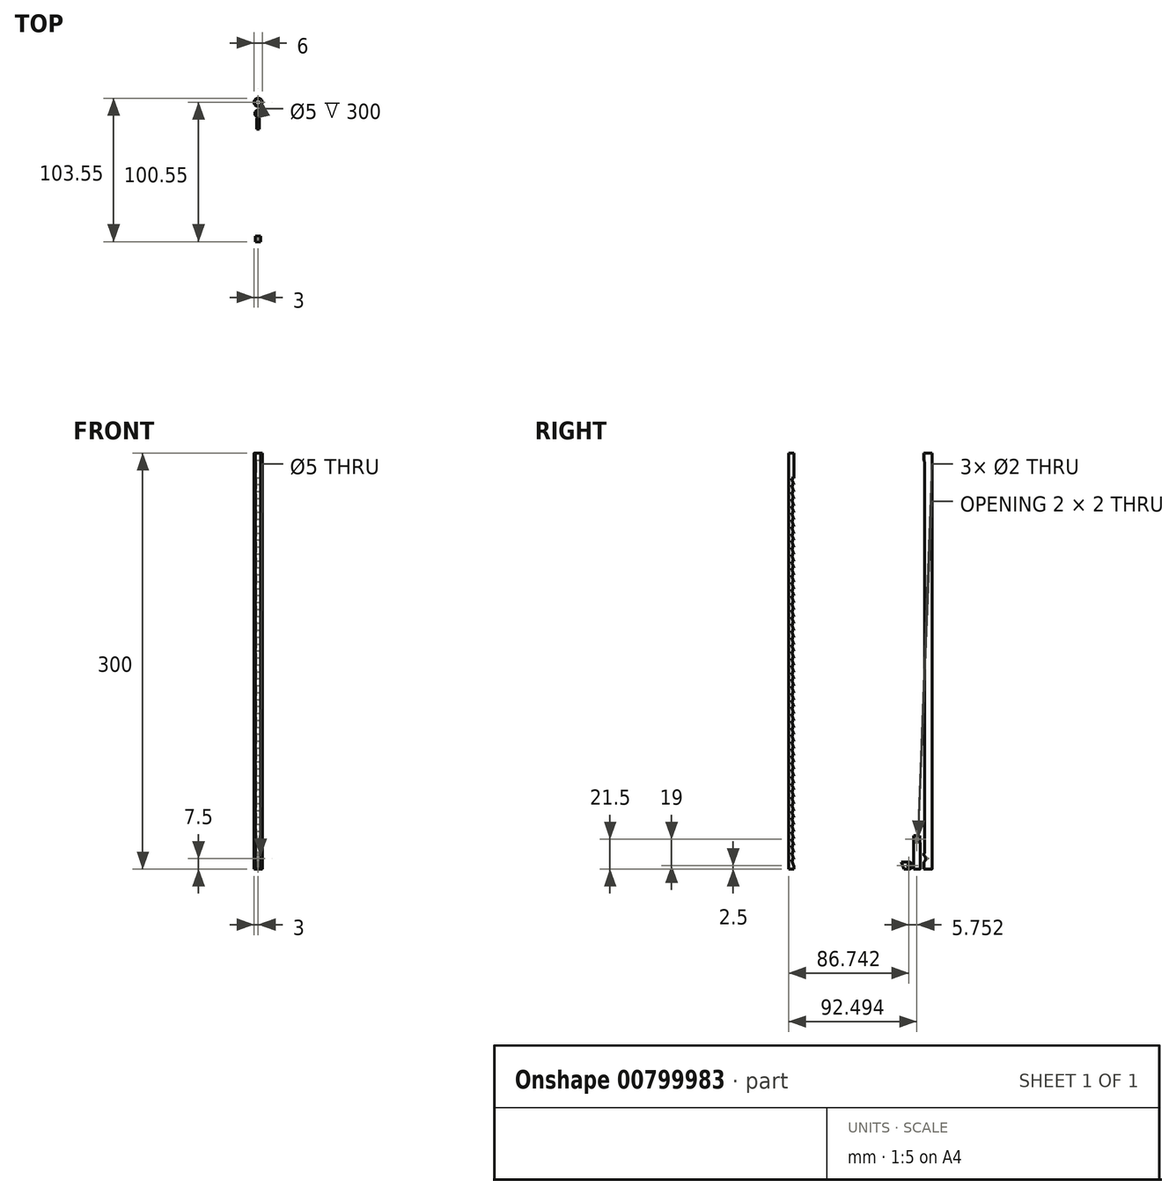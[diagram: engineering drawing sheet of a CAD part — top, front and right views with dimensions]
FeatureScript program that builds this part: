
annotation { "Feature Type Name" : "Feature", "Feature Type Description" : "" }
export const myFeature = defineFeature(function(context is Context, id is Id, definition is map)
    precondition{}
    {
        {
            var Q0;
            Q0=qCreatedBy(makeId("Top.planeOp"),FACE);
            var sketch = newSketch(context, id + "F0", { "sketchPlane" : qUnion([Q0])});
            skCircle(sketch, "E0", {"center": v(0, 3) * mm, "radius": 3 * mm});
            skCircle(sketch, "E1", {"center": v(0, 3) * mm, "radius": 2.5 * mm});
            skSolve(sketch);
        }
        {
            var Q0;
            Q0 = qSketchRegion(id + "F0", true);
            extrude(context, id + "F1", {"entities" : qUnion([Q0]), "depth" : 300 * mm, "offsetDistance" : 25 * mm});
        }
        {
            var Q0;
            Q0=qCreatedBy(makeId("Front.planeOp"),FACE);
            var sketch = newSketch(context, id + "F2", { "sketchPlane" : qUnion([Q0])});
            skCircle(sketch, "E2", {"center": v(0, 7.5) * mm, "radius": 2.5 * mm});
            skCircle(sketch, "E3", {"center": v(0, 17.5) * mm, "radius": 1.5 * mm});
            skCircle(sketch, "E4", {"center": v(0, 293.5) * mm, "radius": 1.5 * mm});
            skLineSegment(sketch, "E5", {"start": v(0, 0) * mm, "end": v(0, 300) * mm});
            skSolve(sketch);
        }
        {
            var Q0;
            Q0 = qSketchRegion(id + "F0", true);
            var Q1;
            Q1=sQuery(id+"F2.wireOp",EDGE,"E2");
            extrude(context, id + "F3", {"entities" : qUnion([Q0]), "operationType" : NewBodyOperationType.REMOVE, "surfaceEntities" : qUnion([Q1]), "oppositeDirection" : true, "depth" : 25 * mm, "offsetDistance" : 25 * mm});
        }
        {
            var Q0;
            Q0=sQuery(id+"F2.wireOp",VERTEX,"E2.center");
            var Q1;
            Q1=makeQuery(id+"F1.opExtrude","SWEPT_BODY",BODY,{"disambiguationData":[OSD([sQuery(id+"F0.wireOp",EDGE,"E0"),sQuery(id+"F0.wireOp",EDGE,"E1")])]});
            hole(context, id + "F4", {"style" : HoleStyle.SIMPLE, "endStyle" : HoleEndStyle.BLIND, "holeDiameter" : 5 * mm, "majorDiameter" : 5 * mm, "holeDepth" : 2 * mm, "isTappedThrough" : true, "tappedDepth" : 12 * mm, "tapClearance" : 3, "locations" : qUnion([Q0]), "scope" : qUnion([Q1])});
        }
        {
            var Q0;
            Q0 = qSketchRegion(id + "F2", true);
            var sketch = newSketch(context, id + "F5", { "sketchPlane" : qUnion([Q0])});
            skLineSegment(sketch, "E6.bottom", {"start": v(-1.5, 11.4) * mm, "end": v(1.5, 11.4) * mm});
            skLineSegment(sketch, "E6.top", {"start": v(-1.5, 293.43) * mm, "end": v(1.5, 293.43) * mm});
            skLineSegment(sketch, "E6.left", {"start": v(-1.5, 11.4) * mm, "end": v(-1.5, 293.43) * mm});
            skLineSegment(sketch, "E6.right", {"start": v(1.5, 11.4) * mm, "end": v(1.5, 293.43) * mm});
            skLineSegment(sketch, "E7", {"start": v(0, 10) * mm, "end": v(0, 300) * mm});
            skLineSegment(sketch, "E8", {"start": v(0, 0) * mm, "end": v(0, 5) * mm});
            skSolve(sketch);
        }
        {
            var Q0;
            {var subQ0=sQuery(id+"F2.wireOp",EDGE,"E5");var subQ1=sQuery(id+"F2.wireOp",EDGE,"E3");var subQ2=makeQuery(id+"F2.imprint","INTERSECT",VERTEX,{"disambiguationData":[OD(0.0)],"derivedFrom":[subQ1,subQ0]});Q0=makeQuery(id+"F2.imprint","IMPRINT",FACE,{"disambiguationData":[TD([[makeQuery(id+"F2.imprint","IMPRINT",EDGE,{"disambiguationData":[TD([[subQ2,1.0]])],"derivedFrom":subQ1}),1.0]])]});}
            var Q1;
            {var subQ0=sQuery(id+"F2.wireOp",EDGE,"E5");var subQ1=sQuery(id+"F2.wireOp",EDGE,"E3");var subQ2=makeQuery(id+"F2.imprint","INTERSECT",VERTEX,{"disambiguationData":[OD(0.0)],"derivedFrom":[subQ1,subQ0]});var subQ5=makeQuery(id+"F2.imprint","IMPRINT",EDGE,{"disambiguationData":[TD([[subQ2,1.0]])],"derivedFrom":subQ1});var subQ9=sQuery(id+"F5.wireOp",EDGE,"E6.left");var subQ10=makeQuery(id+"F5.imprint","INTERSECT",VERTEX,{"disambiguationData":[OD(1.0)],"derivedFrom":[subQ5,subQ9]});Q1=makeQuery(id+"F5.imprint","IMPRINT",FACE,{"disambiguationData":[TD([[makeQuery(id+"F5.imprint","IMPRINT",EDGE,{"disambiguationData":[TD([[subQ10,-1.0]])],"derivedFrom":subQ9}),-1.0]])]});}
            var Q2;
            {var subQ0=sQuery(id+"F2.wireOp",EDGE,"E5");var subQ1=sQuery(id+"F2.wireOp",EDGE,"E3");var subQ2=makeQuery(id+"F2.imprint","INTERSECT",VERTEX,{"disambiguationData":[OD(0.0)],"derivedFrom":[subQ1,subQ0]});Q2=makeQuery(id+"F2.imprint","IMPRINT",FACE,{"disambiguationData":[TD([[makeQuery(id+"F2.imprint","IMPRINT",EDGE,{"disambiguationData":[TD([[subQ2,-1.0]])],"derivedFrom":subQ1}),1.0]])]});}
            extrude(context, id + "F6", {"entities" : qUnion([Q0, Q1, Q2]), "operationType" : NewBodyOperationType.REMOVE, "depth" : 2 * mm, "offsetDistance" : 25 * mm});
        }
        {
            var Q0;
            {var subQ0=sQuery(id+"F2.wireOp",EDGE,"E5");var subQ1=sQuery(id+"F2.wireOp",EDGE,"E3");var subQ2=makeQuery(id+"F2.imprint","INTERSECT",VERTEX,{"disambiguationData":[OD(0.0)],"derivedFrom":[subQ1,subQ0]});Q0=makeQuery(id+"F2.imprint","IMPRINT",FACE,{"disambiguationData":[TD([[makeQuery(id+"F2.imprint","IMPRINT",EDGE,{"disambiguationData":[TD([[subQ2,-1.0]])],"derivedFrom":subQ1}),1.0]])]});}
            var Q1;
            {var subQ0=sQuery(id+"F2.wireOp",EDGE,"E5");var subQ1=sQuery(id+"F2.wireOp",EDGE,"E3");var subQ2=makeQuery(id+"F2.imprint","INTERSECT",VERTEX,{"disambiguationData":[OD(0.0)],"derivedFrom":[subQ1,subQ0]});Q1=makeQuery(id+"F2.imprint","IMPRINT",FACE,{"disambiguationData":[TD([[makeQuery(id+"F2.imprint","IMPRINT",EDGE,{"disambiguationData":[TD([[subQ2,1.0]])],"derivedFrom":subQ1}),1.0]])]});}
            var Q2;
            {var subQ0=sQuery(id+"F5.wireOp",EDGE,"E6.right");var subQ1=sQuery(id+"F2.wireOp",EDGE,"E5");var subQ7=sQuery(id+"F2.wireOp",EDGE,"E3");var subQ8=makeQuery(id+"F2.imprint","INTERSECT",VERTEX,{"disambiguationData":[OD(0.0)],"derivedFrom":[subQ7,subQ1]});var subQ10=makeQuery(id+"F2.imprint","IMPRINT",EDGE,{"disambiguationData":[TD([[subQ8,-1.0]])],"derivedFrom":subQ7});var subQ11=makeQuery(id+"F5.imprint","INTERSECT",VERTEX,{"disambiguationData":[OD(1.0)],"derivedFrom":[subQ10,subQ0]});Q2=makeQuery(id+"F5.imprint","IMPRINT",FACE,{"disambiguationData":[TD([[makeQuery(id+"F5.imprint","IMPRINT",EDGE,{"disambiguationData":[TD([[subQ11,-1.0]])],"derivedFrom":subQ0}),1.0]])]});}
            var Q3;
            {var subQ0=sQuery(id+"F5.wireOp",EDGE,"E6.left");var subQ1=sQuery(id+"F2.wireOp",EDGE,"E5");var subQ7=sQuery(id+"F2.wireOp",EDGE,"E3");var subQ8=makeQuery(id+"F2.imprint","INTERSECT",VERTEX,{"disambiguationData":[OD(0.0)],"derivedFrom":[subQ7,subQ1]});var subQ10=makeQuery(id+"F2.imprint","IMPRINT",EDGE,{"disambiguationData":[TD([[subQ8,1.0]])],"derivedFrom":subQ7});var subQ11=makeQuery(id+"F5.imprint","INTERSECT",VERTEX,{"disambiguationData":[OD(1.0)],"derivedFrom":[subQ10,subQ0]});Q3=makeQuery(id+"F5.imprint","IMPRINT",FACE,{"disambiguationData":[TD([[makeQuery(id+"F5.imprint","IMPRINT",EDGE,{"disambiguationData":[TD([[subQ11,-1.0]])],"derivedFrom":subQ0}),-1.0]])]});}
            var Q4;
            {var subQ0=sQuery(id+"F2.wireOp",EDGE,"E5");var subQ1=sQuery(id+"F2.wireOp",EDGE,"E4");var subQ2=makeQuery(id+"F2.imprint","INTERSECT",VERTEX,{"disambiguationData":[OD(0.0)],"derivedFrom":[subQ1,subQ0]});Q4=makeQuery(id+"F2.imprint","IMPRINT",FACE,{"disambiguationData":[TD([[makeQuery(id+"F2.imprint","IMPRINT",EDGE,{"disambiguationData":[TD([[subQ2,-1.0]])],"derivedFrom":subQ1}),1.0]])]});}
            var Q5;
            {var subQ0=sQuery(id+"F2.wireOp",EDGE,"E5");var subQ1=sQuery(id+"F2.wireOp",EDGE,"E4");var subQ2=makeQuery(id+"F2.imprint","INTERSECT",VERTEX,{"disambiguationData":[OD(0.0)],"derivedFrom":[subQ1,subQ0]});Q5=makeQuery(id+"F2.imprint","IMPRINT",FACE,{"disambiguationData":[TD([[makeQuery(id+"F2.imprint","IMPRINT",EDGE,{"disambiguationData":[TD([[subQ2,1.0]])],"derivedFrom":subQ1}),1.0]])]});}
            extrude(context, id + "F7", {"entities" : qUnion([Q0, Q1, Q2, Q3, Q4, Q5]), "operationType" : NewBodyOperationType.REMOVE, "oppositeDirection" : true, "depth" : 2 * mm, "offsetDistance" : 25 * mm});
        }
        {
            var Q0;
            Q0=qCreatedBy(makeId("Top.planeOp"),FACE);
            var sketch = newSketch(context, id + "F8", { "sketchPlane" : qUnion([Q0])});
            skCircle(sketch, "E9", {"center": v(0, -5.06) * mm, "radius": 2.45 * mm});
            skSolve(sketch);
        }
        {
            var Q0;
            Q0 = qSketchRegion(id + "F8", true);
            extrude(context, id + "F9", {"entities" : qUnion([Q0]), "depth" : 24 * mm, "offsetDistance" : 25 * mm});
        }
        {
            var Q0;
            Q0=makeQuery(id+"F9.opExtrude","CAP_FACE",FACE,{"disambiguationData":[OSD([sQuery(id+"F8.wireOp",EDGE,"E9")])],"isStart":false});
            var sketch = newSketch(context, id + "F10", { "sketchPlane" : qUnion([Q0])});
            skLineSegment(sketch, "E10.bottom", {"start": v(1, -8.94) * mm, "end": v(-1, -8.94) * mm});
            skLineSegment(sketch, "E10.top", {"start": v(1, -1.17) * mm, "end": v(-1, -1.17) * mm});
            skLineSegment(sketch, "E10.left", {"start": v(1, -8.94) * mm, "end": v(1, -1.17) * mm});
            skLineSegment(sketch, "E10.right", {"start": v(-1, -8.94) * mm, "end": v(-1, -1.17) * mm});
            skPoint(sketch, "E10.middle", {"position": v(0, -5.06) * mm});
            skSolve(sketch);
        }
        {
            var Q0;
            Q0 = qSketchRegion(id + "F10", true);
            extrude(context, id + "F11", {"entities" : qUnion([Q0]), "operationType" : NewBodyOperationType.REMOVE, "oppositeDirection" : true, "depth" : 5 * mm, "offsetDistance" : 25 * mm});
        }
        {
            var Q0;
            Q0=qCreatedBy(makeId("Right.planeOp"),FACE);
            var sketch = newSketch(context, id + "F12", { "sketchPlane" : qUnion([Q0])});
            skCircle(sketch, "E11", {"center": v(-5.06, 21.5) * mm, "radius": 1 * mm});
            skLineSegment(sketch, "E12", {"start": v(-2.6, 19) * mm, "end": v(-2.6, 0) * mm});
            skLineSegment(sketch, "E13", {"start": v(-7.5, 0) * mm, "end": v(-7.5, 19) * mm});
            skSolve(sketch);
        }
        {
            var Q0;
            Q0 = qSketchRegion(id + "F12", true);
            extrude(context, id + "F13", {"entities" : qUnion([Q0]), "operationType" : NewBodyOperationType.REMOVE, "depth" : 25 * mm, "offsetDistance" : 25 * mm, "hasSecondDirection" : true, "secondDirectionOppositeDirection" : true, "secondDirectionDepth" : 25 * mm});
        }
        {
            var Q0;
            Q0=qCreatedBy(makeId("Top.planeOp"),FACE);
            var sketch = newSketch(context, id + "F14", { "sketchPlane" : qUnion([Q0])});
            skLineSegment(sketch, "E14.bottom", {"start": v(1, -16.3) * mm, "end": v(-1, -16.3) * mm});
            skLineSegment(sketch, "E14.top", {"start": v(1, -8.3) * mm, "end": v(-1, -8.3) * mm});
            skLineSegment(sketch, "E14.left", {"start": v(1, -16.3) * mm, "end": v(1, -8.3) * mm});
            skLineSegment(sketch, "E14.right", {"start": v(-1, -16.3) * mm, "end": v(-1, -8.3) * mm});
            skPoint(sketch, "E14.middle", {"position": v(0, -12.3) * mm});
            skSolve(sketch);
        }
        {
            var Q0;
            Q0 = qSketchRegion(id + "F14", true);
            extrude(context, id + "F15", {"entities" : qUnion([Q0]), "depth" : 5 * mm, "offsetDistance" : 25 * mm});
        }
        {
            var Q0;
            Q0=makeQuery(id+"F15.opExtrude","SWEPT_FACE",FACE,{"disambiguationData":[OSD([sQuery(id+"F14.wireOp",EDGE,"E14.left")])]});
            cPlane(context, id + "F16", {"entities" : qUnion([Q0]), "cplaneType" : CPlaneType.OFFSET, "offset" : 0 * mm, "width" : 150 * mm, "height" : 150 * mm});
        }
        {
            var Q0;
            Q0=qCreatedBy(id+"F16.planeOp",FACE);
            var sketch = newSketch(context, id + "F17", { "sketchPlane" : qUnion([Q0])});
            skCircle(sketch, "E15", {"center": v(-10.8, 2.5) * mm, "radius": 2.5 * mm});
            skSolve(sketch);
        }
        {
            var Q0;
            Q0=makeQuery(id+"F15.opExtrude","CAP_EDGE",EDGE,{"disambiguationData":[OSD([sQuery(id+"F14.wireOp",EDGE,"E14.top")])],"isStart":true});
            var Q1;
            Q1=makeQuery(id+"F15.opExtrude","CAP_EDGE",EDGE,{"disambiguationData":[OSD([sQuery(id+"F14.wireOp",EDGE,"E14.top")])],"isStart":false});
            fillet(context, id + "F18", {"entities" : qUnion([Q0, Q1]), "radius" : 2.5 * mm, "tangentPropagation" : true, "allowEdgeOverflow" : false});
        }
        {
            var Q0;
            Q0=sQuery(id+"F17.wireOp",VERTEX,"E15.center");
            var Q1;
            Q1=makeQuery(id+"F15.opExtrude","SWEPT_BODY",BODY,{"disambiguationData":[OSD([sQuery(id+"F14.wireOp",EDGE,"E14.bottom"),sQuery(id+"F14.wireOp",EDGE,"E14.top"),sQuery(id+"F14.wireOp",EDGE,"E14.left"),sQuery(id+"F14.wireOp",EDGE,"E14.right")])]});
            hole(context, id + "F19", {"style" : HoleStyle.SIMPLE, "endStyle" : HoleEndStyle.THROUGH, "holeDiameter" : 2 * mm, "majorDiameter" : 5 * mm, "isTappedThrough" : true, "tappedDepth" : 12 * mm, "tapClearance" : 3, "locations" : qUnion([Q0]), "scope" : qUnion([Q1])});
        }
        {
            var Q0;
            Q0=makeQuery(id+"F15.opExtrude","CAP_EDGE",EDGE,{"disambiguationData":[OSD([sQuery(id+"F14.wireOp",EDGE,"E14.bottom")])],"isStart":true});
            chamfer(context, id + "F20", {"entities" : qUnion([Q0]), "chamferType" : ChamferType.TWO_OFFSETS, "width1" : 2 * mm, "oppositeDirection" : false, "width2" : 5 * mm, "tangentPropagation" : true});
        }
        {
            var Q0;
            Q0=qCreatedBy(makeId("Right.planeOp"),FACE);
            var sketch = newSketch(context, id + "F21", { "sketchPlane" : qUnion([Q0])});
            skLineSegment(sketch, "E16.bottom", {"start": v(-97.55, 0) * mm, "end": v(-93.65, 0) * mm});
            skLineSegment(sketch, "E16.top", {"start": v(-97.55, 300) * mm, "end": v(-93.65, 300) * mm});
            skLineSegment(sketch, "E16.left", {"start": v(-97.55, 0) * mm, "end": v(-97.55, 300) * mm});
            skLineSegment(sketch, "E16.right", {"start": v(-93.65, 0) * mm, "end": v(-93.65, 300) * mm});
            skLineSegment(sketch, "E17", {"start": v(-93.65, 7) * mm, "end": v(-95.65, 7) * mm});
            skLineSegment(sketch, "E18", {"start": v(-95.65, 7) * mm, "end": v(-93.65, 2) * mm});
            skLineSegment(sketch, "E19.0.1.0", {"start": v(-93.65, 12) * mm, "end": v(-95.65, 12) * mm});
            skLineSegment(sketch, "E19.0.1.1", {"start": v(-95.65, 12) * mm, "end": v(-93.65, 7) * mm});
            skLineSegment(sketch, "E19.0.2.0", {"start": v(-93.65, 17) * mm, "end": v(-95.65, 17) * mm});
            skLineSegment(sketch, "E19.0.2.1", {"start": v(-95.65, 17) * mm, "end": v(-93.65, 12) * mm});
            skLineSegment(sketch, "E19.0.3.0", {"start": v(-93.65, 22) * mm, "end": v(-95.65, 22) * mm});
            skLineSegment(sketch, "E19.0.3.1", {"start": v(-95.65, 22) * mm, "end": v(-93.65, 17) * mm});
            skLineSegment(sketch, "E19.0.4.0", {"start": v(-93.65, 27) * mm, "end": v(-95.65, 27) * mm});
            skLineSegment(sketch, "E19.0.4.1", {"start": v(-95.65, 27) * mm, "end": v(-93.65, 22) * mm});
            skLineSegment(sketch, "E19.0.5.0", {"start": v(-93.65, 32) * mm, "end": v(-95.65, 32) * mm});
            skLineSegment(sketch, "E19.0.5.1", {"start": v(-95.65, 32) * mm, "end": v(-93.65, 27) * mm});
            skLineSegment(sketch, "E19.0.6.0", {"start": v(-93.65, 37) * mm, "end": v(-95.65, 37) * mm});
            skLineSegment(sketch, "E19.0.6.1", {"start": v(-95.65, 37) * mm, "end": v(-93.65, 32) * mm});
            skLineSegment(sketch, "E19.0.7.0", {"start": v(-93.65, 42) * mm, "end": v(-95.65, 42) * mm});
            skLineSegment(sketch, "E19.0.7.1", {"start": v(-95.65, 42) * mm, "end": v(-93.65, 37) * mm});
            skLineSegment(sketch, "E19.0.8.0", {"start": v(-93.65, 47) * mm, "end": v(-95.65, 47) * mm});
            skLineSegment(sketch, "E19.0.8.1", {"start": v(-95.65, 47) * mm, "end": v(-93.65, 42) * mm});
            skLineSegment(sketch, "E19.0.9.0", {"start": v(-93.65, 52) * mm, "end": v(-95.65, 52) * mm});
            skLineSegment(sketch, "E19.0.9.1", {"start": v(-95.65, 52) * mm, "end": v(-93.65, 47) * mm});
            skLineSegment(sketch, "E19.0.10.0", {"start": v(-93.65, 57) * mm, "end": v(-95.65, 57) * mm});
            skLineSegment(sketch, "E19.0.10.1", {"start": v(-95.65, 57) * mm, "end": v(-93.65, 52) * mm});
            skLineSegment(sketch, "E19.0.11.0", {"start": v(-93.65, 62) * mm, "end": v(-95.65, 62) * mm});
            skLineSegment(sketch, "E19.0.11.1", {"start": v(-95.65, 62) * mm, "end": v(-93.65, 57) * mm});
            skLineSegment(sketch, "E19.0.12.0", {"start": v(-93.65, 67) * mm, "end": v(-95.65, 67) * mm});
            skLineSegment(sketch, "E19.0.12.1", {"start": v(-95.65, 67) * mm, "end": v(-93.65, 62) * mm});
            skLineSegment(sketch, "E19.0.13.0", {"start": v(-93.65, 72) * mm, "end": v(-95.65, 72) * mm});
            skLineSegment(sketch, "E19.0.13.1", {"start": v(-95.65, 72) * mm, "end": v(-93.65, 67) * mm});
            skLineSegment(sketch, "E19.0.14.0", {"start": v(-93.65, 77) * mm, "end": v(-95.65, 77) * mm});
            skLineSegment(sketch, "E19.0.14.1", {"start": v(-95.65, 77) * mm, "end": v(-93.65, 72) * mm});
            skLineSegment(sketch, "E19.0.15.0", {"start": v(-93.65, 82) * mm, "end": v(-95.65, 82) * mm});
            skLineSegment(sketch, "E19.0.15.1", {"start": v(-95.65, 82) * mm, "end": v(-93.65, 77) * mm});
            skLineSegment(sketch, "E19.0.16.0", {"start": v(-93.65, 87) * mm, "end": v(-95.65, 87) * mm});
            skLineSegment(sketch, "E19.0.16.1", {"start": v(-95.65, 87) * mm, "end": v(-93.65, 82) * mm});
            skLineSegment(sketch, "E19.0.17.0", {"start": v(-93.65, 92) * mm, "end": v(-95.65, 92) * mm});
            skLineSegment(sketch, "E19.0.17.1", {"start": v(-95.65, 92) * mm, "end": v(-93.65, 87) * mm});
            skLineSegment(sketch, "E19.0.18.0", {"start": v(-93.65, 97) * mm, "end": v(-95.65, 97) * mm});
            skLineSegment(sketch, "E19.0.18.1", {"start": v(-95.65, 97) * mm, "end": v(-93.65, 92) * mm});
            skLineSegment(sketch, "E19.0.19.0", {"start": v(-93.65, 102) * mm, "end": v(-95.65, 102) * mm});
            skLineSegment(sketch, "E19.0.19.1", {"start": v(-95.65, 102) * mm, "end": v(-93.65, 97) * mm});
            skLineSegment(sketch, "E19.0.20.0", {"start": v(-93.65, 107) * mm, "end": v(-95.65, 107) * mm});
            skLineSegment(sketch, "E19.0.20.1", {"start": v(-95.65, 107) * mm, "end": v(-93.65, 102) * mm});
            skLineSegment(sketch, "E19.0.21.0", {"start": v(-93.65, 112) * mm, "end": v(-95.65, 112) * mm});
            skLineSegment(sketch, "E19.0.21.1", {"start": v(-95.65, 112) * mm, "end": v(-93.65, 107) * mm});
            skLineSegment(sketch, "E19.0.22.0", {"start": v(-93.65, 117) * mm, "end": v(-95.65, 117) * mm});
            skLineSegment(sketch, "E19.0.22.1", {"start": v(-95.65, 117) * mm, "end": v(-93.65, 112) * mm});
            skLineSegment(sketch, "E19.0.23.0", {"start": v(-93.65, 122) * mm, "end": v(-95.65, 122) * mm});
            skLineSegment(sketch, "E19.0.23.1", {"start": v(-95.65, 122) * mm, "end": v(-93.65, 117) * mm});
            skLineSegment(sketch, "E19.0.24.0", {"start": v(-93.65, 127) * mm, "end": v(-95.65, 127) * mm});
            skLineSegment(sketch, "E19.0.24.1", {"start": v(-95.65, 127) * mm, "end": v(-93.65, 122) * mm});
            skLineSegment(sketch, "E19.0.25.0", {"start": v(-93.65, 132) * mm, "end": v(-95.65, 132) * mm});
            skLineSegment(sketch, "E19.0.25.1", {"start": v(-95.65, 132) * mm, "end": v(-93.65, 127) * mm});
            skLineSegment(sketch, "E19.0.26.0", {"start": v(-93.65, 137) * mm, "end": v(-95.65, 137) * mm});
            skLineSegment(sketch, "E19.0.26.1", {"start": v(-95.65, 137) * mm, "end": v(-93.65, 132) * mm});
            skLineSegment(sketch, "E19.0.27.0", {"start": v(-93.65, 142) * mm, "end": v(-95.65, 142) * mm});
            skLineSegment(sketch, "E19.0.27.1", {"start": v(-95.65, 142) * mm, "end": v(-93.65, 137) * mm});
            skLineSegment(sketch, "E19.0.28.0", {"start": v(-93.65, 147) * mm, "end": v(-95.65, 147) * mm});
            skLineSegment(sketch, "E19.0.28.1", {"start": v(-95.65, 147) * mm, "end": v(-93.65, 142) * mm});
            skLineSegment(sketch, "E19.0.29.0", {"start": v(-93.65, 152) * mm, "end": v(-95.65, 152) * mm});
            skLineSegment(sketch, "E19.0.29.1", {"start": v(-95.65, 152) * mm, "end": v(-93.65, 147) * mm});
            skLineSegment(sketch, "E19.0.30.0", {"start": v(-93.65, 157) * mm, "end": v(-95.65, 157) * mm});
            skLineSegment(sketch, "E19.0.30.1", {"start": v(-95.65, 157) * mm, "end": v(-93.65, 152) * mm});
            skLineSegment(sketch, "E19.0.31.0", {"start": v(-93.65, 162) * mm, "end": v(-95.65, 162) * mm});
            skLineSegment(sketch, "E19.0.31.1", {"start": v(-95.65, 162) * mm, "end": v(-93.65, 157) * mm});
            skLineSegment(sketch, "E19.0.32.0", {"start": v(-93.65, 167) * mm, "end": v(-95.65, 167) * mm});
            skLineSegment(sketch, "E19.0.32.1", {"start": v(-95.65, 167) * mm, "end": v(-93.65, 162) * mm});
            skLineSegment(sketch, "E19.0.33.0", {"start": v(-93.65, 172) * mm, "end": v(-95.65, 172) * mm});
            skLineSegment(sketch, "E19.0.33.1", {"start": v(-95.65, 172) * mm, "end": v(-93.65, 167) * mm});
            skLineSegment(sketch, "E19.0.34.0", {"start": v(-93.65, 177) * mm, "end": v(-95.65, 177) * mm});
            skLineSegment(sketch, "E19.0.34.1", {"start": v(-95.65, 177) * mm, "end": v(-93.65, 172) * mm});
            skLineSegment(sketch, "E19.0.35.0", {"start": v(-93.65, 182) * mm, "end": v(-95.65, 182) * mm});
            skLineSegment(sketch, "E19.0.35.1", {"start": v(-95.65, 182) * mm, "end": v(-93.65, 177) * mm});
            skLineSegment(sketch, "E19.0.36.0", {"start": v(-93.65, 187) * mm, "end": v(-95.65, 187) * mm});
            skLineSegment(sketch, "E19.0.36.1", {"start": v(-95.65, 187) * mm, "end": v(-93.65, 182) * mm});
            skLineSegment(sketch, "E19.0.37.0", {"start": v(-93.65, 192) * mm, "end": v(-95.65, 192) * mm});
            skLineSegment(sketch, "E19.0.37.1", {"start": v(-95.65, 192) * mm, "end": v(-93.65, 187) * mm});
            skLineSegment(sketch, "E19.0.38.0", {"start": v(-93.65, 197) * mm, "end": v(-95.65, 197) * mm});
            skLineSegment(sketch, "E19.0.38.1", {"start": v(-95.65, 197) * mm, "end": v(-93.65, 192) * mm});
            skLineSegment(sketch, "E19.0.39.0", {"start": v(-93.65, 202) * mm, "end": v(-95.65, 202) * mm});
            skLineSegment(sketch, "E19.0.39.1", {"start": v(-95.65, 202) * mm, "end": v(-93.65, 197) * mm});
            skLineSegment(sketch, "E19.0.40.0", {"start": v(-93.65, 207) * mm, "end": v(-95.65, 207) * mm});
            skLineSegment(sketch, "E19.0.40.1", {"start": v(-95.65, 207) * mm, "end": v(-93.65, 202) * mm});
            skLineSegment(sketch, "E19.0.41.0", {"start": v(-93.65, 212) * mm, "end": v(-95.65, 212) * mm});
            skLineSegment(sketch, "E19.0.41.1", {"start": v(-95.65, 212) * mm, "end": v(-93.65, 207) * mm});
            skLineSegment(sketch, "E19.0.42.0", {"start": v(-93.65, 217) * mm, "end": v(-95.65, 217) * mm});
            skLineSegment(sketch, "E19.0.42.1", {"start": v(-95.65, 217) * mm, "end": v(-93.65, 212) * mm});
            skLineSegment(sketch, "E19.0.43.0", {"start": v(-93.65, 222) * mm, "end": v(-95.65, 222) * mm});
            skLineSegment(sketch, "E19.0.43.1", {"start": v(-95.65, 222) * mm, "end": v(-93.65, 217) * mm});
            skLineSegment(sketch, "E19.0.44.0", {"start": v(-93.65, 227) * mm, "end": v(-95.65, 227) * mm});
            skLineSegment(sketch, "E19.0.44.1", {"start": v(-95.65, 227) * mm, "end": v(-93.65, 222) * mm});
            skLineSegment(sketch, "E19.0.45.0", {"start": v(-93.65, 232) * mm, "end": v(-95.65, 232) * mm});
            skLineSegment(sketch, "E19.0.45.1", {"start": v(-95.65, 232) * mm, "end": v(-93.65, 227) * mm});
            skLineSegment(sketch, "E19.0.46.0", {"start": v(-93.65, 237) * mm, "end": v(-95.65, 237) * mm});
            skLineSegment(sketch, "E19.0.46.1", {"start": v(-95.65, 237) * mm, "end": v(-93.65, 232) * mm});
            skLineSegment(sketch, "E19.0.47.0", {"start": v(-93.65, 242) * mm, "end": v(-95.65, 242) * mm});
            skLineSegment(sketch, "E19.0.47.1", {"start": v(-95.65, 242) * mm, "end": v(-93.65, 237) * mm});
            skLineSegment(sketch, "E19.0.48.0", {"start": v(-93.65, 247) * mm, "end": v(-95.65, 247) * mm});
            skLineSegment(sketch, "E19.0.48.1", {"start": v(-95.65, 247) * mm, "end": v(-93.65, 242) * mm});
            skLineSegment(sketch, "E19.0.49.0", {"start": v(-93.65, 252) * mm, "end": v(-95.65, 252) * mm});
            skLineSegment(sketch, "E19.0.49.1", {"start": v(-95.65, 252) * mm, "end": v(-93.65, 247) * mm});
            skLineSegment(sketch, "E19.0.50.0", {"start": v(-93.65, 257) * mm, "end": v(-95.65, 257) * mm});
            skLineSegment(sketch, "E19.0.50.1", {"start": v(-95.65, 257) * mm, "end": v(-93.65, 252) * mm});
            skLineSegment(sketch, "E19.0.51.0", {"start": v(-93.65, 262) * mm, "end": v(-95.65, 262) * mm});
            skLineSegment(sketch, "E19.0.51.1", {"start": v(-95.65, 262) * mm, "end": v(-93.65, 257) * mm});
            skLineSegment(sketch, "E19.0.52.0", {"start": v(-93.65, 267) * mm, "end": v(-95.65, 267) * mm});
            skLineSegment(sketch, "E19.0.52.1", {"start": v(-95.65, 267) * mm, "end": v(-93.65, 262) * mm});
            skLineSegment(sketch, "E19.0.53.0", {"start": v(-93.65, 272) * mm, "end": v(-95.65, 272) * mm});
            skLineSegment(sketch, "E19.0.53.1", {"start": v(-95.65, 272) * mm, "end": v(-93.65, 267) * mm});
            skLineSegment(sketch, "E19.0.54.0", {"start": v(-93.65, 277) * mm, "end": v(-95.65, 277) * mm});
            skLineSegment(sketch, "E19.0.54.1", {"start": v(-95.65, 277) * mm, "end": v(-93.65, 272) * mm});
            skLineSegment(sketch, "E19.direction1", {"start": v(-95.65, 7) * mm, "end": v(-75.86, 6.3) * mm, "construction": true});
            skLineSegment(sketch, "E19.direction2", {"start": v(-95.65, 7) * mm, "end": v(-95.65, 12) * mm, "construction": true});
            skLineSegment(sketch, "E20.0.0.55", {"start": v(-93.65, 282) * mm, "end": v(-95.65, 282) * mm});
            skLineSegment(sketch, "E20.3.0.55", {"start": v(-95.65, 282) * mm, "end": v(-93.65, 277) * mm});
            skSolve(sketch);
        }
        {
            var Q0;
            {var subQ0=sQuery(id+"F21.wireOp",EDGE,"E16.bottom");Q0=makeQuery(id+"F21.imprint","IMPRINT",FACE,{"disambiguationData":[TD([[makeQuery(id+"F21.imprint","IMPRINT",EDGE,{"derivedFrom":subQ0}),1.0]])]});}
            extrude(context, id + "F22", {"entities" : qUnion([Q0]), "depth" : 1.9 * mm, "offsetDistance" : 25 * mm, "hasSecondDirection" : true, "secondDirectionOppositeDirection" : true, "secondDirectionDepth" : 1.9 * mm});
        }
    });
